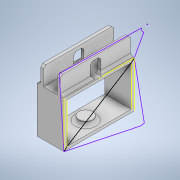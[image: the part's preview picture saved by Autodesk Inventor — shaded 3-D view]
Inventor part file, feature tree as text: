
AUTODESK INVENTOR PART (.ipt)
format: ipt  version: 2020 (Build 240168000, 168)  size: 256,000 bytes
history: native  units: mm
features: sketch x8, extrude x7, chamfer x2, fillet x1
ambient origin geometry x8: Origin, YZ Plane, XZ Plane, XY Plane, X Axis, Y Axis, Z Axis, Center Point
bodies: Solid1 (feature_tree)
feature tree (18):
  extrude  "Extrusion1"  Depth=61.0mm
  extrude  "Extrusion2"  TaperAngle=0.0deg  [1 undecoded]
  extrude  "Extrusion3"  Depth=2.5mm
  extrude  "Extrusion4"  Depth=6.0mm
  extrude  "Extrusion5"  Depth=56.0mm
  extrude  "Extrusion6"  Depth=3.0mm
  extrude  "Extrusion7"  Depth=2.5mm TaperAngle=0.0deg
  chamfer  "Chamfer1"  [1 undecoded]
  chamfer  "Chamfer2"  Distance=2.5mm
  fillet  "Fillet1"  Radius=2.5mm
  sketch  "Sketch10"  dims[d16=0.0mm d17=0.0mm d18=2.5mm d19=2.5mm d20=35.0mm d21=2.5mm d22=0.0mm d23=0.0mm d24=2.5mm d25=0.0mm d26=12.0mm d27=3.0mm d28=6.0mm d29=0.0mm d30=0.0mm d31=7.5mm d32=10.0mm d33=8.0mm d34=0.0mm d35=0.0mm d36=9.0mm d37=4.5mm d38=12.5mm d39=0.0mm d40=2.0mm d41=2.0mm d42=45.0deg d43=2.0mm d44=2.0mm d45=45.0deg d46=3.0mm d49=0.5mm d50=0.872665mm d51=0.5mm d52=0.872665mm]
  sketch  "Sketch1"  dims[d0=61.0mm d1=30.5mm]
  sketch  "Sketch2"  dims[d2=0.0mm d3=0.0mm]
  sketch  "Sketch3"  dims[d4=2.5mm d5=2.5mm]
  sketch  "Sketch4"  dims[d6=12.0mm d7=6.0mm]
  sketch  "Sketch5"  dims[d8=15.5mm d9=0.0mm d10=56.0mm]
  sketch  "Sketch6"  dims[d11=28.0mm d12=3.0mm]
  sketch  "Sketch7"  dims[d13=3.0mm d14=2.5mm d15=0.0mm]
note: 2 required parameter values undecoded (feature->parameter linkage not recoverable at this tier; creation-order binding heuristic only, values carry confidence <= 0.55)
